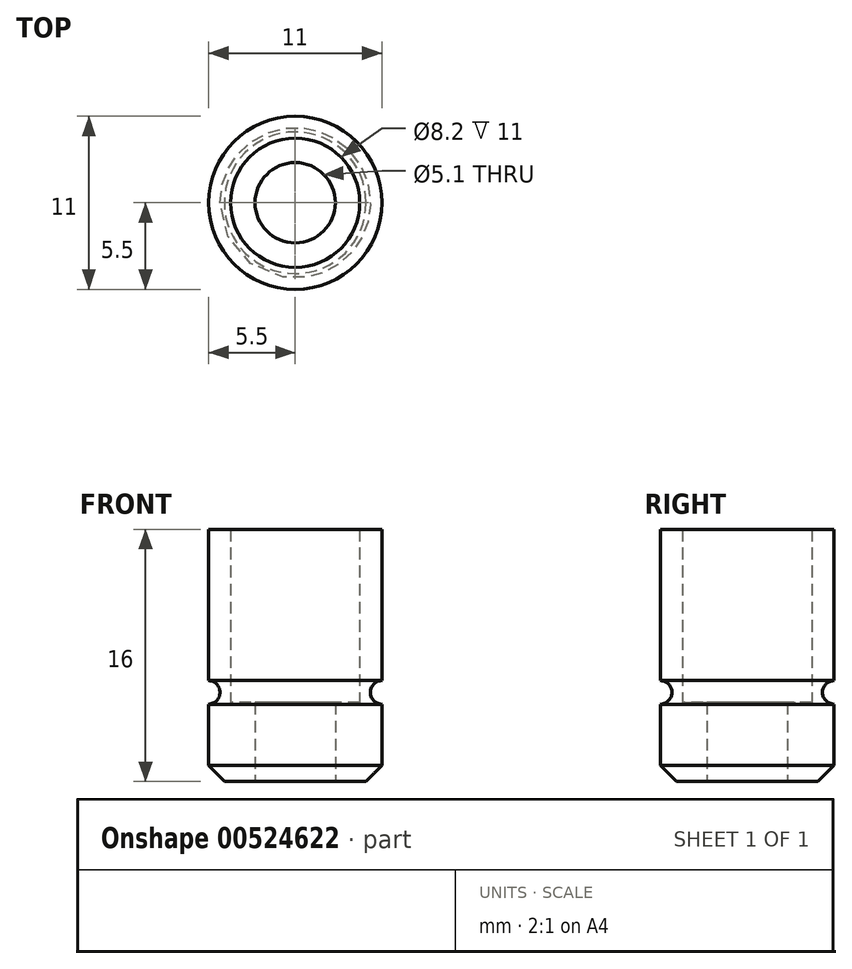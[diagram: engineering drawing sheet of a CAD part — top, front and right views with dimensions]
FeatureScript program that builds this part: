
annotation { "Feature Type Name" : "Feature", "Feature Type Description" : "" }
export const myFeature = defineFeature(function(context is Context, id is Id, definition is map)
    precondition{}
    {
        {
            var Q0;
            Q0=qCreatedBy(makeId("Top.planeOp"),FACE);
            var sketch = newSketch(context, id + "F0", { "sketchPlane" : qUnion([Q0])});
            skCircle(sketch, "E0", {"center": v(0, 0) * mm, "radius": 2.55 * mm});
            skCircle(sketch, "E1", {"center": v(0, 0) * mm, "radius": 4.1 * mm});
            skCircle(sketch, "E2", {"center": v(0, 0) * mm, "radius": 5.5 * mm});
            skSolve(sketch);
        }
        {
            var Q0;
            Q0=makeQuery(id+"F0.imprint","IMPRINT",FACE,{"disambiguationData":[TD([[makeQuery(id+"F0.imprint","IMPRINT",EDGE,{"derivedFrom":sQuery(id+"F0.wireOp",EDGE,"E1")}),-1.0]])]});
            extrude(context, id + "F1", {"entities" : qUnion([Q0]), "depth" : 16 * mm, "offsetDistance" : 25 * mm});
        }
        {
            var Q0;
            Q0=makeQuery(id+"F0.imprint","IMPRINT",FACE,{"disambiguationData":[TD([[makeQuery(id+"F0.imprint","IMPRINT",EDGE,{"derivedFrom":sQuery(id+"F0.wireOp",EDGE,"E0")}),-1.0]])]});
            extrude(context, id + "F2", {"entities" : qUnion([Q0]), "operationType" : NewBodyOperationType.ADD, "depth" : 5 * mm, "offsetDistance" : 25 * mm});
        }
        {
            var Q0;
            Q0=makeQuery(id+"F1.opExtrude","CAP_EDGE",EDGE,{"disambiguationData":[OSD([sQuery(id+"F0.wireOp",EDGE,"E2")])],"isStart":true});
            chamfer(context, id + "F3", {"entities" : qUnion([Q0]), "width" : 1 * mm, "tangentPropagation" : true});
        }
        {
            var Q0;
            Q0=qCreatedBy(makeId("Front.planeOp"),FACE);
            var sketch = newSketch(context, id + "F4", { "sketchPlane" : qUnion([Q0])});
            skCircle(sketch, "E3", {"center": v(5.53, 5.65) * mm, "radius": 0.75 * mm});
            skSolve(sketch);
        }
        {
            var Q0;
            Q0=makeQuery(id+"F4.imprint","IMPRINT",FACE,{"disambiguationData":[TD([[makeQuery(id+"F4.imprint","IMPRINT",EDGE,{"derivedFrom":sQuery(id+"F4.wireOp",EDGE,"E3")}),1.0]])]});
            var Q1;
            Q1=makeQuery(id+"F1.opExtrude","SWEPT_FACE",FACE,{"disambiguationData":[OSD([sQuery(id+"F0.wireOp",EDGE,"E2")])]});
            revolve(context, id + "F5", {"operationType" : NewBodyOperationType.REMOVE, "entities" : qUnion([Q0]), "axis" : qUnion([Q1]), "revolveType" : RevolveType.FULL, "oppositeDirection" : true});
        }
    });
